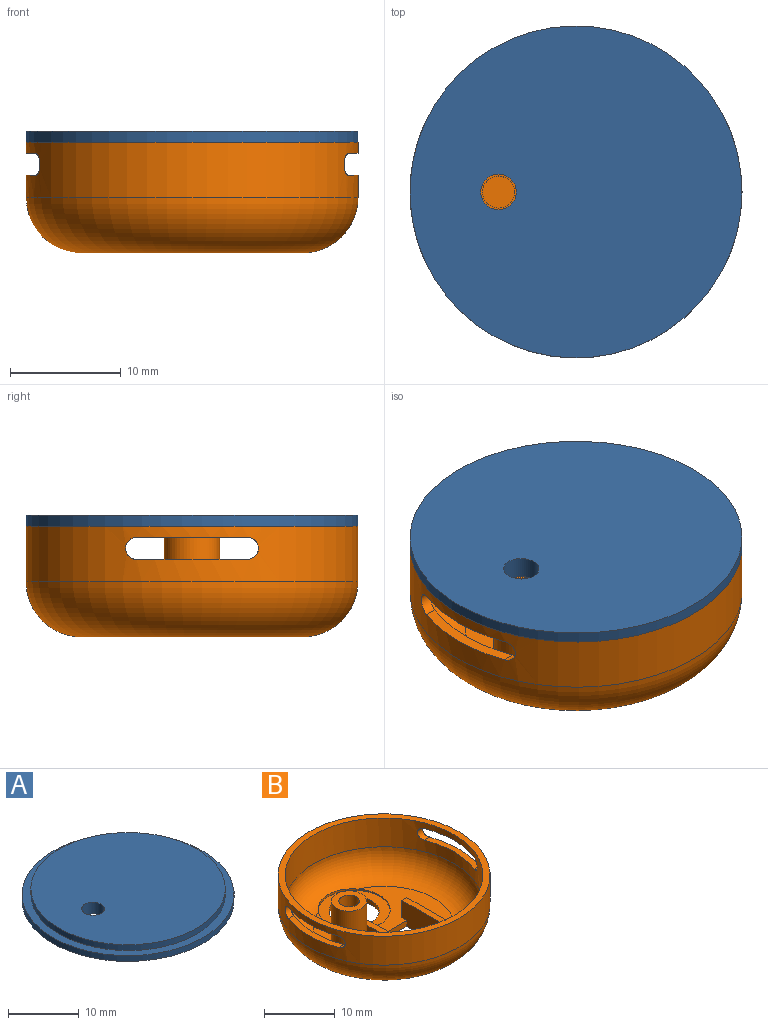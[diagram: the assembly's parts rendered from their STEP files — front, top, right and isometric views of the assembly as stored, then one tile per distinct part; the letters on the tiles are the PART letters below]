
ASSEMBLY  parts=2 mates=1
PART A: 6 faces, bbox 30x30x2 mm
  f0: cylinder r=13.75mm len=27.5mm, axis (0,0,-1), area 86.4mm2, adj f1,f3
  f1: plane 27.5x27.5mm, normal (0,0,1), area 585.9mm2, adj f0,f5
  f2: cylinder r=15mm len=30mm, axis (0,0,-1), area 94.2mm2, adj f3,f4
  f3: plane 30x30mm, normal (0,0,1), area 112.9mm2, adj f0,f2
  f4: plane 30x30mm, normal (0,0,-1), area 698.8mm2, adj f2,f5
  f5: cylinder r=1.6mm len=3.2mm, axis (0,0,1), area 20.1mm2, adj f1,f4
PART B: 33 faces, bbox 32.5x32.5x10 mm
  f0: cylinder r=15mm len=30mm, axis (0,0,-1), area 423.7mm2, adj f6,f7,f25,f26,f27,f28,f29,f30
  f1: cylinder r=14mm len=28mm, axis (0,0,-1), area 392.1mm2, adj f3,f6,f25,f26,f27,f28,f29,f30
  f2: plane 20x18.16mm, normal (0,0,1), area 142.2mm2, adj f3,f9,f10,f11,f13,f15,f17,f18
  f3: torus R=10mm, axis (0,0,1), area 487.1mm2, adj f1,f2,f5,f13,f15,f16,f17
  f4: plane 20x20mm, normal (0,0,-1), area 222.2mm2, adj f7,f8,f9,f10,f11,f12
  f5: plane 3.17x0.13mm, normal (0,0,1), area 0.3mm2, adj f3,f16
  f6: plane 30x30mm, normal (0,0,1), area 91.1mm2, adj f0,f1
  f7: torus R=10mm, axis (0,0,1), area 650.6mm2, adj f0,f4
  f8: plane 6.8x4mm, normal (0,1,0), area 27.2mm2, adj f4,f9,f11,f20
  f9: plane 8.7x4mm, normal (-1,0,0), area 33.8mm2, adj f2,f4,f8,f10,f19,f20
  f10: plane 6.8x1mm, normal (0,-1,0), area 6.8mm2, adj f2,f4,f9,f11
  f11: plane 8.7x4mm, normal (1,0,0), area 33.8mm2, adj f2,f4,f8,f10,f18,f20
  f12: cylinder r=3.55mm len=7.1mm, axis (0,0,1), area 16.7mm2, adj f4,f14
  f13: cylinder r=5.1mm len=10.2mm, axis (0,0,1), area 8.7mm2, adj f2,f3,f14
  f14: plane 10.2x10.2mm, normal (0,0,1), area 42.1mm2, adj f12,f13
  f15: plane 9.72x3.02mm, normal (-1,0,0), area 29.1mm2, adj f2,f3,f16,f18,f20
  f16: plane 8.8x3mm, normal (0,-1,0), area 26.3mm2, adj f3,f5,f15,f17,f20
  f17: plane 9.72x3.02mm, normal (1,0,0), area 29.1mm2, adj f2,f3,f16,f19,f20
  f18: plane 3x1mm, normal (0,1,0), area 3mm2, adj f2,f11,f15,f20
  f19: plane 3x1mm, normal (0,1,0), area 3mm2, adj f2,f9,f17,f20
  f20: plane 9.7x8.8mm, normal (0,0,1), area 26.2mm2, adj f8,f9,f11,f15,f16,f17,f18,f19
  f21: cylinder r=1.45mm len=8mm, axis (0,0,-1), area 72.9mm2, adj f23,f24
  f22: cylinder r=2.5mm len=8mm, axis (0,0,-1), area 125.7mm2, adj f2,f23
  f23: plane 5x5mm, normal (0,0,1), area 13mm2, adj f21,f22
  f24: plane 2.9x2.9mm, normal (0,0,1), area 6.6mm2, adj f21
  f25: plane 10x1.92mm, normal (0,0,-1), area 10.2mm2, adj f0,f1,f26,f28
  f26: cylinder r=1mm len=2mm, axis (-1,0,0), area 3.4mm2, adj f0,f1,f25,f27
  f27: plane 10x1.92mm, normal (0,0,1), area 10.2mm2, adj f0,f1,f26,f28
  f28: cylinder r=1mm len=2mm, axis (-1,0,0), area 3.4mm2, adj f0,f1,f25,f27
  f29: cylinder r=1mm len=2mm, axis (1,0,0), area 3.4mm2, adj f0,f1,f30,f31
  f30: plane 10x1.92mm, normal (0,0,1), area 10.2mm2, adj f0,f1,f29,f32
  f31: plane 10x1.92mm, normal (0,0,-1), area 10.2mm2, adj f0,f1,f29,f32
  f32: cylinder r=1mm len=2mm, axis (1,0,0), area 3.4mm2, adj f0,f1,f30,f31
PLACE A rot(axis=(1,0,0),180deg) t=(-91.86,-2.51,9.35)mm
PLACE B t=(-31.8,-2.51,-1.65)mm
MATE slider A.f5 <-> B.f21  axis (0,0,1) through (-38.8,-2.51,9.35)mm
